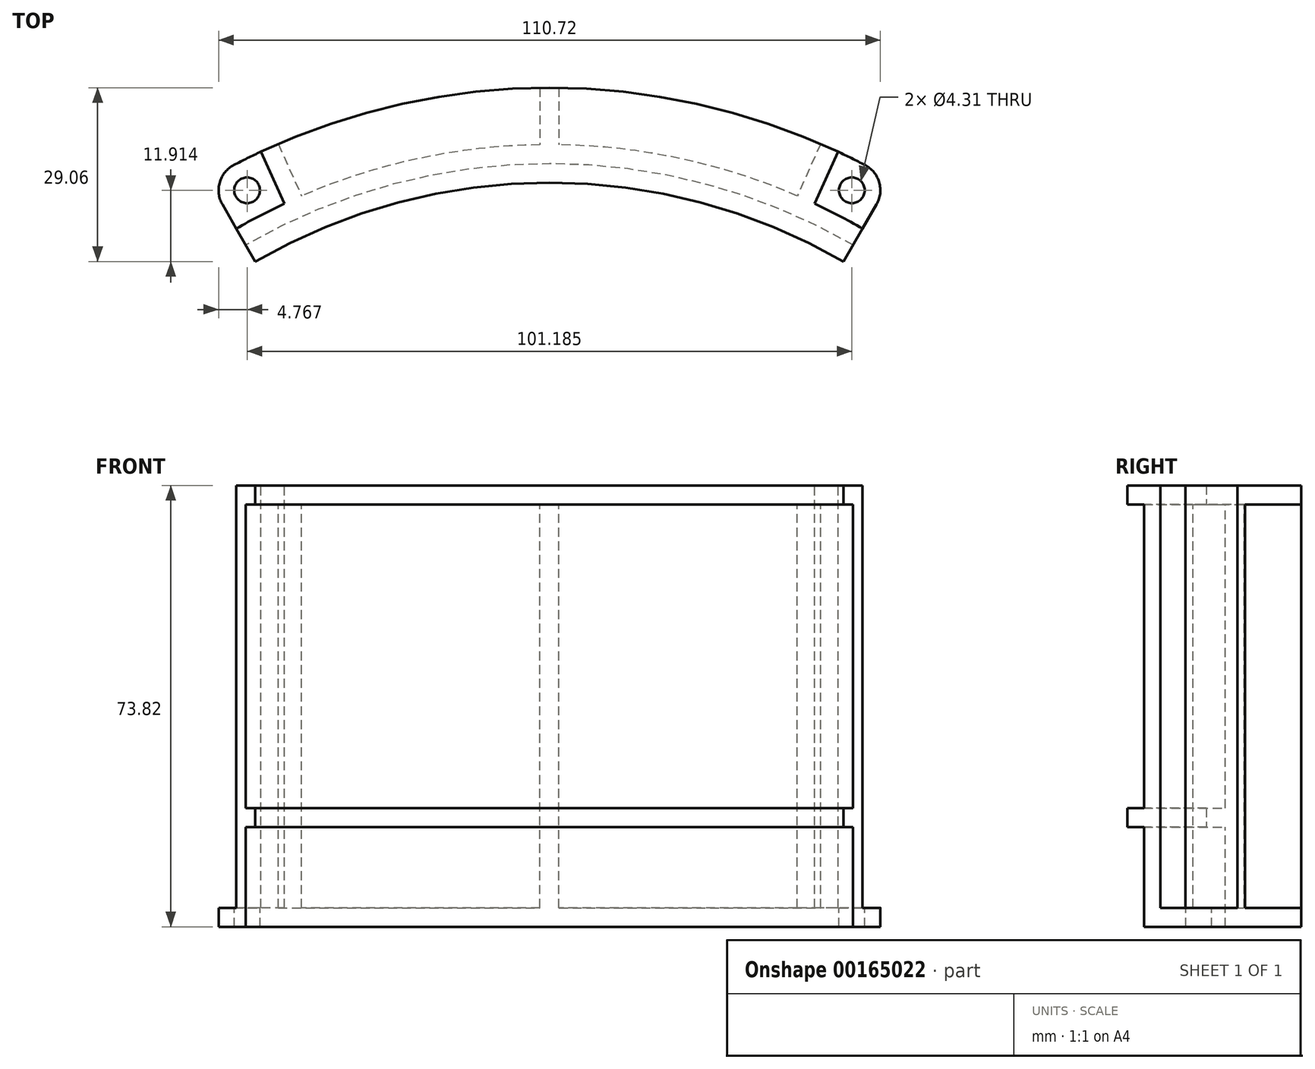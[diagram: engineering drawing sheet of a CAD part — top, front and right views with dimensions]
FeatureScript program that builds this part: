
annotation { "Feature Type Name" : "Feature", "Feature Type Description" : "" }
export const myFeature = defineFeature(function(context is Context, id is Id, definition is map)
    precondition{}
    {
        {
            var Q0;
            Q0=qCreatedBy(makeId("Top.planeOp"),FACE);
            var sketch = newSketch(context, id + "F0", { "sketchPlane" : qUnion([Q0])});
            skLineSegment(sketch, "E0", {"start": v(0, 0) * mm, "end": v(-49.21, 85.24) * mm, "construction": true});
            skLineSegment(sketch, "E1", {"start": v(0, 0) * mm, "end": v(49.21, 85.24) * mm, "construction": true});
            skLineSegment(sketch, "E2", {"start": v(0, 0) * mm, "end": v(0, 98.42) * mm, "construction": true});
            skArc(sketch, "E3", {"start": v(49.21, 85.24) * mm, "mid": v(0, 98.42) * mm, "end": v(-49.21, 85.24) * mm});
            skLineSegment(sketch, "E4", {"start": v(-49.21, 85.24) * mm, "end": v(-57.15, 98.99) * mm});
            skLineSegment(sketch, "E5", {"start": v(49.21, 85.24) * mm, "end": v(57.15, 98.99) * mm});
            skArc(sketch, "E6", {"start": v(57.15, 98.99) * mm, "mid": v(0, 114.3) * mm, "end": v(-57.15, 98.99) * mm});
            skSolve(sketch);
        }
        {
            var Q0;
            Q0 = qSketchRegion(id + "F0", true);
            extrude(context, id + "F1", {"entities" : qUnion([Q0]), "depth" : 70.64 * mm});
        }
        {
            var Q0;
            Q0=makeQuery(id+"F1.opExtrude","SWEPT_FACE",FACE,{"disambiguationData":[OSD([sQuery(id+"F0.wireOp",EDGE,"E4")])]});
            var sketch = newSketch(context, id + "F2", { "sketchPlane" : qUnion([Q0])});
            skLineSegment(sketch, "E7.bottom", {"start": v(-98.42, 67.47) * mm, "end": v(-101.6, 67.47) * mm});
            skLineSegment(sketch, "E7.top", {"start": v(-98.42, 16.67) * mm, "end": v(-101.6, 16.67) * mm});
            skLineSegment(sketch, "E7.left", {"start": v(-98.42, 67.47) * mm, "end": v(-98.42, 16.67) * mm});
            skLineSegment(sketch, "E7.right", {"start": v(-101.6, 67.47) * mm, "end": v(-101.6, 16.67) * mm});
            skLineSegment(sketch, "E8", {"start": v(-101.6, 67.47) * mm, "end": v(-101.6, 70.64) * mm, "construction": true});
            skLineSegment(sketch, "E9.bottom", {"start": v(-98.42, 0) * mm, "end": v(-101.6, 0) * mm});
            skLineSegment(sketch, "E9.top", {"start": v(-98.42, 13.5) * mm, "end": v(-101.6, 13.5) * mm});
            skLineSegment(sketch, "E9.left", {"start": v(-98.42, 0) * mm, "end": v(-98.42, 13.5) * mm});
            skLineSegment(sketch, "E9.right", {"start": v(-101.6, 0) * mm, "end": v(-101.6, 13.5) * mm});
            skLineSegment(sketch, "E10", {"start": v(-101.6, 16.67) * mm, "end": v(-101.6, 13.5) * mm, "construction": true});
            skSolve(sketch);
        }
        {
            var Q0;
            Q0=makeQuery(id+"F2.imprint","IMPRINT",FACE,{"disambiguationData":[TD([[makeQuery(id+"F2.imprint","IMPRINT",EDGE,{"derivedFrom":sQuery(id+"F2.wireOp",EDGE,"E7.bottom")}),1.0]])]});
            var Q1;
            Q1=makeQuery(id+"F2.imprint","IMPRINT",FACE,{"disambiguationData":[TD([[makeQuery(id+"F2.imprint","IMPRINT",EDGE,{"derivedFrom":sQuery(id+"F2.wireOp",EDGE,"E9.bottom")}),-1.0]])]});
            var Q2;
            Q2=makeQuery(id+"F1.opExtrude","SWEPT_FACE",FACE,{"disambiguationData":[OSD([sQuery(id+"F0.wireOp",EDGE,"E3")])]});
            revolve(context, id + "F3", {"operationType" : NewBodyOperationType.REMOVE, "entities" : qUnion([Q0, Q1]), "axis" : qUnion([Q2]), "revolveType" : RevolveType.FULL, "oppositeDirection" : true});
        }
        {
            var Q0;
            Q0=makeQuery(id+"F1.opExtrude","CAP_FACE",FACE,{"disambiguationData":[OSD([sQuery(id+"F0.wireOp",EDGE,"E3"),sQuery(id+"F0.wireOp",EDGE,"E4"),sQuery(id+"F0.wireOp",EDGE,"E5"),sQuery(id+"F0.wireOp",EDGE,"E6")])],"isStart":false});
            var sketch = newSketch(context, id + "F4", { "sketchPlane" : qUnion([Q0])});
            skLineSegment(sketch, "E11", {"start": v(-57.15, 98.99) * mm, "end": v(-52.39, 90.74) * mm});
            skLineSegment(sketch, "E12", {"start": v(-48.27, 103.6) * mm, "end": v(-44.37, 94.92) * mm});
            skArc(sketch, "E13", {"start": v(-44.37, 94.92) * mm, "mid": v(-48.42, 92.91) * mm, "end": v(-52.39, 90.74) * mm});
            skCircle(sketch, "E14", {"center": v(-50.6, 97.15) * mm, "radius": 4.76 * mm, "construction": true});
            skLineSegment(sketch, "E15", {"start": v(0, 0) * mm, "end": v(0, 104.76) * mm, "construction": true});
            skLineSegment(sketch, "E16", {"start": v(-41.47, 96.22) * mm, "end": v(-45.37, 104.9) * mm});
            skLineSegment(sketch, "E17", {"start": v(-44.37, 94.92) * mm, "end": v(-41.47, 96.22) * mm, "construction": true});
            skArc(sketch, "E18", {"start": v(-48.27, 103.6) * mm, "mid": v(-52.76, 101.4) * mm, "end": v(-57.15, 98.99) * mm});
            skLineSegment(sketch, "E19", {"start": v(-48.27, 103.6) * mm, "end": v(-45.37, 104.9) * mm, "construction": true});
            skArc(sketch, "E20", {"start": v(-1.59, 114.29) * mm, "mid": v(-23.94, 111.76) * mm, "end": v(-45.37, 104.9) * mm});
            skArc(sketch, "E21", {"start": v(-1.59, 104.76) * mm, "mid": v(-21.95, 102.45) * mm, "end": v(-41.47, 96.22) * mm});
            skLineSegment(sketch, "E22.bottom", {"start": v(-1.59, 104.76) * mm, "end": v(1.59, 104.76) * mm, "construction": true});
            skLineSegment(sketch, "E22.top", {"start": v(-1.59, 114.29) * mm, "end": v(1.59, 114.29) * mm, "construction": true});
            skLineSegment(sketch, "E22.left", {"start": v(-1.59, 104.76) * mm, "end": v(-1.59, 114.29) * mm});
            skLineSegment(sketch, "E22.right", {"start": v(1.59, 104.76) * mm, "end": v(1.59, 114.29) * mm});
            skArc(sketch, "E23", {"start": v(41.47, 96.22) * mm, "mid": v(21.95, 102.45) * mm, "end": v(1.59, 104.76) * mm});
            skArc(sketch, "E24", {"start": v(45.37, 104.9) * mm, "mid": v(23.94, 111.76) * mm, "end": v(1.59, 114.29) * mm});
            skArc(sketch, "E25", {"start": v(52.39, 90.74) * mm, "mid": v(48.42, 92.91) * mm, "end": v(44.37, 94.92) * mm});
            skLineSegment(sketch, "E26", {"start": v(52.39, 90.74) * mm, "end": v(57.15, 98.99) * mm});
            skCircle(sketch, "E27", {"center": v(50.6, 97.15) * mm, "radius": 4.76 * mm, "construction": true});
            skLineSegment(sketch, "E28.bottom", {"start": v(48.27, 103.6) * mm, "end": v(45.37, 104.9) * mm, "construction": true});
            skLineSegment(sketch, "E28.top", {"start": v(44.37, 94.92) * mm, "end": v(41.47, 96.22) * mm, "construction": true});
            skLineSegment(sketch, "E28.left", {"start": v(44.37, 94.92) * mm, "end": v(48.27, 103.6) * mm});
            skLineSegment(sketch, "E28.right", {"start": v(41.47, 96.22) * mm, "end": v(45.37, 104.9) * mm});
            skLineSegment(sketch, "E29", {"start": v(-42.92, 95.57) * mm, "end": v(0, 0) * mm, "construction": true});
            skLineSegment(sketch, "E30", {"start": v(0, 0) * mm, "end": v(42.92, 95.57) * mm, "construction": true});
            skArc(sketch, "E31", {"start": v(57.15, 98.99) * mm, "mid": v(52.76, 101.4) * mm, "end": v(48.27, 103.6) * mm});
            skSolve(sketch);
        }
        {
            var Q0;
            Q0 = qSketchRegion(id + "F4", true);
            var Q1;
            Q1=makeQuery(id+"F1.opExtrude","CAP_FACE",FACE,{"disambiguationData":[OSD([sQuery(id+"F0.wireOp",EDGE,"E3"),sQuery(id+"F0.wireOp",EDGE,"E4"),sQuery(id+"F0.wireOp",EDGE,"E5"),sQuery(id+"F0.wireOp",EDGE,"E6")])],"isStart":true});
            extrude(context, id + "F5", {"entities" : qUnion([Q0]), "operationType" : NewBodyOperationType.REMOVE, "endBound" : BoundingType.UP_TO_SURFACE, "oppositeDirection" : true, "endBoundEntityFace" : qUnion([Q1]), "depth" : 25.4 * mm});
        }
        {
            var Q0;
            Q0=makeQuery(id+"F1.opExtrude","CAP_FACE",FACE,{"disambiguationData":[OSD([sQuery(id+"F0.wireOp",EDGE,"E3"),sQuery(id+"F0.wireOp",EDGE,"E4"),sQuery(id+"F0.wireOp",EDGE,"E5"),sQuery(id+"F0.wireOp",EDGE,"E6")])],"isStart":true});
            var sketch = newSketch(context, id + "F6", { "sketchPlane" : qUnion([Q0])});
            skLineSegment(sketch, "E32", {"start": v(-50.8, -87.99) * mm, "end": v(-54.72, -94.77) * mm});
            skLineSegment(sketch, "E33", {"start": v(50.8, -87.99) * mm, "end": v(54.72, -94.77) * mm});
            skArc(sketch, "E34", {"start": v(-52.8, -101.38) * mm, "mid": v(0, -114.3) * mm, "end": v(52.8, -101.38) * mm});
            skArc(sketch, "E35", {"start": v(52.8, -101.38) * mm, "mid": v(55.16, -98.49) * mm, "end": v(54.72, -94.77) * mm});
            skArc(sketch, "E36", {"start": v(54.72, -94.77) * mm, "mid": v(46.02, -95.82) * mm, "end": v(52.8, -101.38) * mm, "construction": true});
            skArc(sketch, "E37", {"start": v(-54.72, -94.77) * mm, "mid": v(-55.16, -98.49) * mm, "end": v(-52.8, -101.38) * mm});
            skCircle(sketch, "E38", {"center": v(50.6, -97.15) * mm, "radius": 2.15 * mm});
            skCircle(sketch, "E39", {"center": v(-50.6, -97.15) * mm, "radius": 2.15 * mm});
            skArc(sketch, "E40", {"start": v(-50.8, -87.99) * mm, "mid": v(0, -101.6) * mm, "end": v(50.8, -87.99) * mm});
            skSolve(sketch);
        }
        {
            var Q0;
            Q0 = qSketchRegion(id + "F6", true);
            extrude(context, id + "F7", {"entities" : qUnion([Q0]), "operationType" : NewBodyOperationType.ADD, "depth" : 3.17 * mm});
        }
        {
            var Q0;
            Q0=makeQuery(id+"F1.opExtrude","CAP_FACE",FACE,{"disambiguationData":[OSD([sQuery(id+"F0.wireOp",EDGE,"E3"),sQuery(id+"F0.wireOp",EDGE,"E4"),sQuery(id+"F0.wireOp",EDGE,"E5"),sQuery(id+"F0.wireOp",EDGE,"E6")])],"isStart":false});
            var sketch = newSketch(context, id + "F8", { "sketchPlane" : qUnion([Q0])});
            skLineSegment(sketch, "E41", {"start": v(48.27, 103.6) * mm, "end": v(44.37, 94.92) * mm});
            skArc(sketch, "E42", {"start": v(44.37, 94.92) * mm, "mid": v(0, 104.77) * mm, "end": v(-44.37, 94.92) * mm});
            skArc(sketch, "E43", {"start": v(48.27, 103.6) * mm, "mid": v(0, 114.3) * mm, "end": v(-48.27, 103.6) * mm});
            skLineSegment(sketch, "E44", {"start": v(-44.37, 94.92) * mm, "end": v(-48.27, 103.6) * mm});
            skSolve(sketch);
        }
        {
            var Q0;
            Q0 = qSketchRegion(id + "F8", true);
            extrude(context, id + "F9", {"entities" : qUnion([Q0]), "operationType" : NewBodyOperationType.ADD, "oppositeDirection" : true, "depth" : 3.17 * mm});
        }
    });
